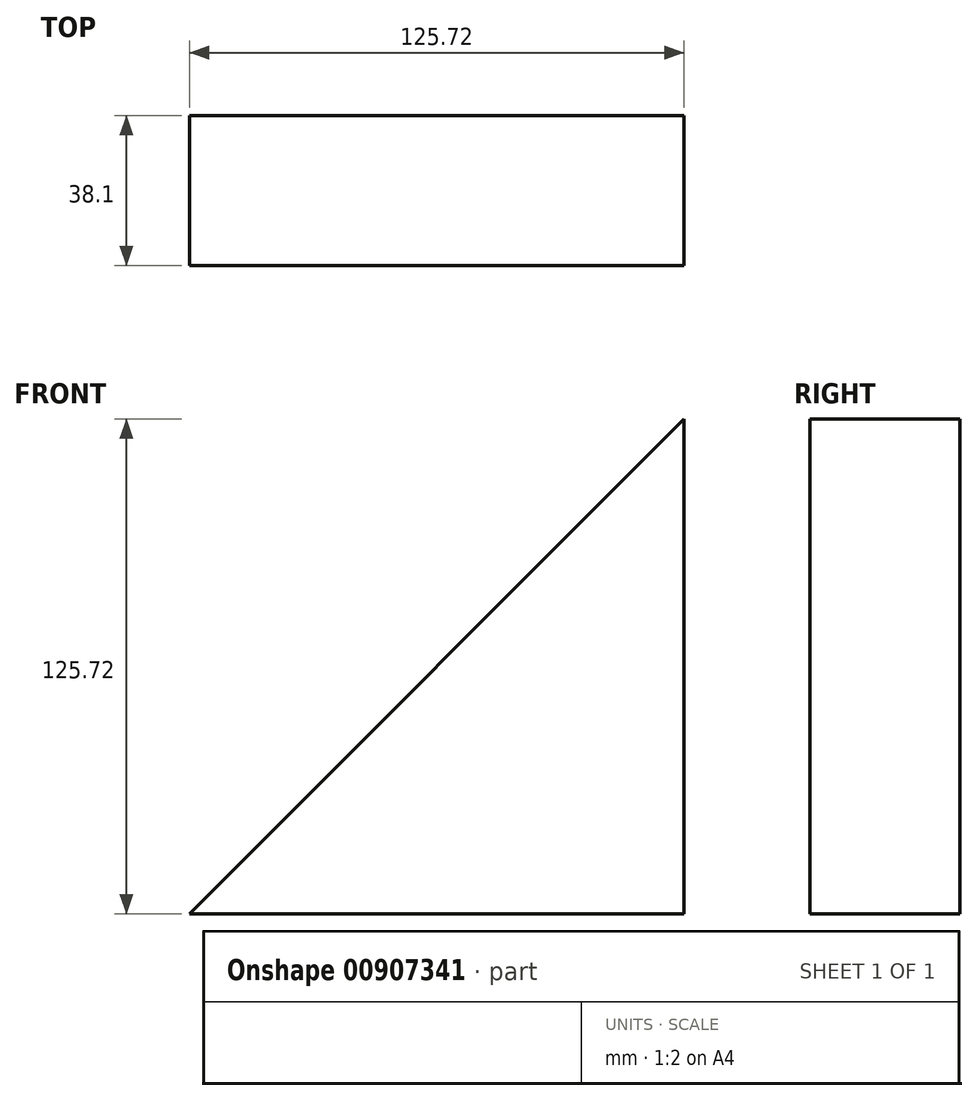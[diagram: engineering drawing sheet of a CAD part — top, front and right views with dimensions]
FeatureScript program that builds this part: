
annotation { "Feature Type Name" : "Feature", "Feature Type Description" : "" }
export const myFeature = defineFeature(function(context is Context, id is Id, definition is map)
    precondition{}
    {
        {
            var Q0;
            Q0=qCreatedBy(makeId("Front.planeOp"),FACE);
            var sketch = newSketch(context, id + "F0", { "sketchPlane" : qUnion([Q0])});
            skLineSegment(sketch, "E0.bottom", {"start": v(-44.45, 19.05) * mm, "end": v(44.45, 19.05) * mm});
            skLineSegment(sketch, "E0.top", {"start": v(-44.45, -19.05) * mm, "end": v(44.45, -19.05) * mm});
            skLineSegment(sketch, "E0.left", {"start": v(-44.45, 19.05) * mm, "end": v(-44.45, -19.05) * mm});
            skLineSegment(sketch, "E0.right", {"start": v(44.45, 19.05) * mm, "end": v(44.45, -19.05) * mm});
            skPoint(sketch, "E0.middle", {"position": v(0, 0) * mm});
            skSolve(sketch);
        }
        {
            var Q0;
            Q0=makeQuery(id+"F0.imprint","IMPRINT",FACE,{"disambiguationData":[TD([[makeQuery(id+"F0.imprint","IMPRINT",EDGE,{"derivedFrom":sQuery(id+"F0.wireOp",EDGE,"E0.bottom")}),-1.0]])]});
            extrude(context, id + "F1", {"entities" : qUnion([Q0]), "endBound" : BoundingType.SYMMETRIC, "depth" : 177.8 * mm, "offsetDistance" : 25.4 * mm});
        }
        {
            var Q0;
            Q0=makeQuery(id+"F1.opExtrude","CAP_EDGE",EDGE,{"disambiguationData":[OSD([sQuery(id+"F0.wireOp",EDGE,"E0.right")])],"isStart":false});
            var Q1;
            Q1=makeQuery(id+"F1.opExtrude","CAP_EDGE",EDGE,{"disambiguationData":[OSD([sQuery(id+"F0.wireOp",EDGE,"E0.right")])],"isStart":true});
            chamfer(context, id + "F2", {"entities" : qUnion([Q0, Q1]), "width" : 88.9 * mm, "tangentPropagation" : true});
        }
        {
            var Q0;
            Q0=makeQuery(id+"F1.opExtrude","SWEPT_BODY",BODY,{"disambiguationData":[OSD([sQuery(id+"F0.wireOp",EDGE,"E0.bottom"),sQuery(id+"F0.wireOp",EDGE,"E0.top"),sQuery(id+"F0.wireOp",EDGE,"E0.left"),sQuery(id+"F0.wireOp",EDGE,"E0.right")])]});
            var Q1;
            Q1=makeQuery(id+"F2.opChamfer","BLEND_EDGE",EDGE,{"blendedFrom":[makeQuery(id+"F1.opExtrude","CAP_EDGE",EDGE,{"disambiguationData":[OSD([sQuery(id+"F0.wireOp",EDGE,"E0.right")])],"isStart":false}),makeQuery(id+"F1.opExtrude","SWEPT_FACE",FACE,{"disambiguationData":[OSD([sQuery(id+"F0.wireOp",EDGE,"E0.bottom")])]})],"blendedInto":[makeQuery(id+"F1.opExtrude","SWEPT_FACE",FACE,{"disambiguationData":[OSD([sQuery(id+"F0.wireOp",EDGE,"E0.bottom")])]})]});
            transform(context, id + "F3", {"entities" : qUnion([Q0]), "transformType" : TransformType.ROTATION, "transformAxis" : qUnion([Q1]), "angle" : 90 * degree, "oppositeDirection" : true, "makeCopy" : false});
        }
        {
            var Q0;
            Q0=makeQuery(id+"F1.opExtrude","SWEPT_BODY",BODY,{"disambiguationData":[OSD([sQuery(id+"F0.wireOp",EDGE,"E0.bottom"),sQuery(id+"F0.wireOp",EDGE,"E0.top"),sQuery(id+"F0.wireOp",EDGE,"E0.left"),sQuery(id+"F0.wireOp",EDGE,"E0.right")])]});
            var Q1;
            Q1=makeQuery(id+"F2.opChamfer","BLEND_EDGE",EDGE,{"blendedFrom":[makeQuery(id+"F1.opExtrude","CAP_EDGE",EDGE,{"disambiguationData":[OSD([sQuery(id+"F0.wireOp",EDGE,"E0.right")])],"isStart":true}),makeQuery(id+"F1.opExtrude","SWEPT_FACE",FACE,{"disambiguationData":[OSD([sQuery(id+"F0.wireOp",EDGE,"E0.top")])]})],"blendedInto":[makeQuery(id+"F1.opExtrude","SWEPT_FACE",FACE,{"disambiguationData":[OSD([sQuery(id+"F0.wireOp",EDGE,"E0.top")])]})]});
            transform(context, id + "F4", {"entities" : qUnion([Q0]), "transformType" : TransformType.ROTATION, "transformAxis" : qUnion([Q1]), "angle" : 45 * degree, "makeCopy" : false});
        }
    });
